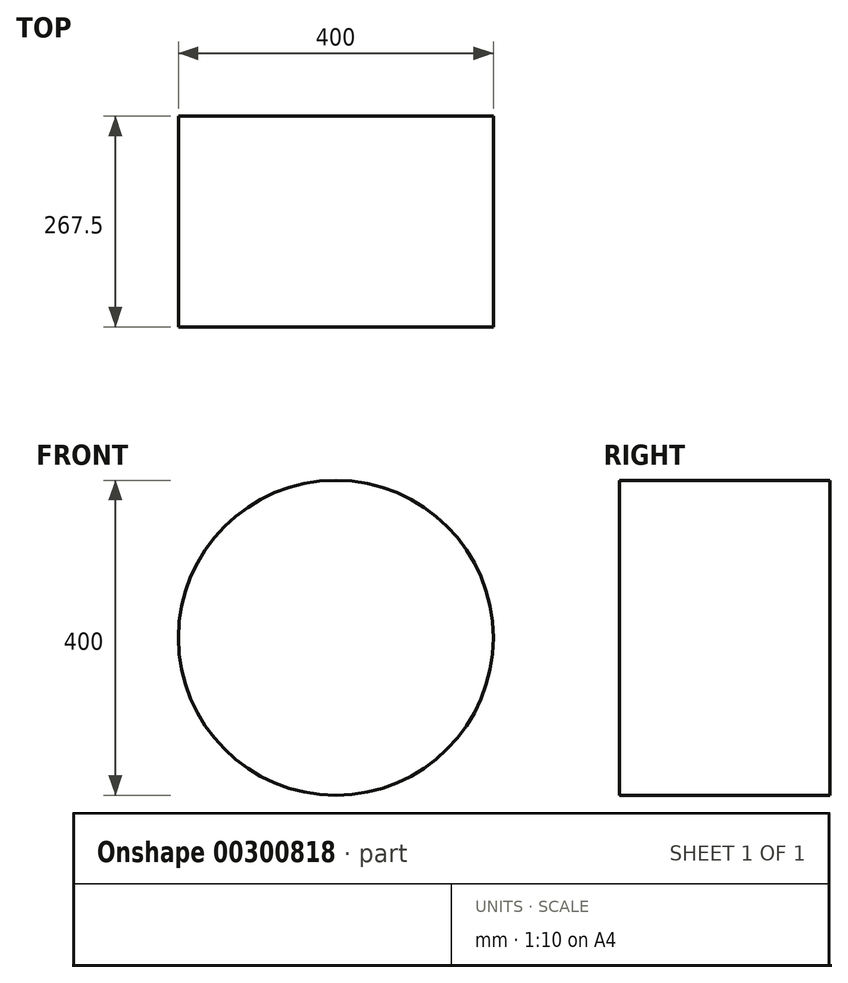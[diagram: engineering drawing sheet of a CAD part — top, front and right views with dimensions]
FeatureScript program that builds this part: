
annotation { "Feature Type Name" : "Feature", "Feature Type Description" : "" }
export const myFeature = defineFeature(function(context is Context, id is Id, definition is map)
    precondition{}
    {
        {
            var Q0;
            Q0=qCreatedBy(makeId("Front.planeOp"),FACE);
            var sketch = newSketch(context, id + "F0", { "sketchPlane" : qUnion([Q0])});
            skCircle(sketch, "E0", {"center": v(0, 0) * mm, "radius": 400 * mm});
            skSolve(sketch);
        }
        {
            var Q0;
            Q0=makeQuery(id+"F0.imprint","IMPRINT",FACE,{"disambiguationData":[TD([[makeQuery(id+"F0.imprint","IMPRINT",EDGE,{"derivedFrom":sQuery(id+"F0.wireOp",EDGE,"E0")}),1.0]])]});
            extrude(context, id + "F1", {"entities" : qUnion([Q0]), "depth" : 535 * mm});
        }
        {
            var Q0;
            Q0=makeQuery(id+"F1.opExtrude","SWEPT_BODY",BODY,{"disambiguationData":[OSD([sQuery(id+"F0.wireOp",EDGE,"E0")])]});
            var Q1;
            Q1=qCreatedBy(makeId("Origin.pointOp"),VERTEX);
            transform(context, id + "F2", {"entities" : qUnion([Q0]), "transformType" : TransformType.SCALE_UNIFORMLY, "scale" : 0.5, "scalePoint" : qUnion([Q1]), "makeCopy" : false});
        }
    });
